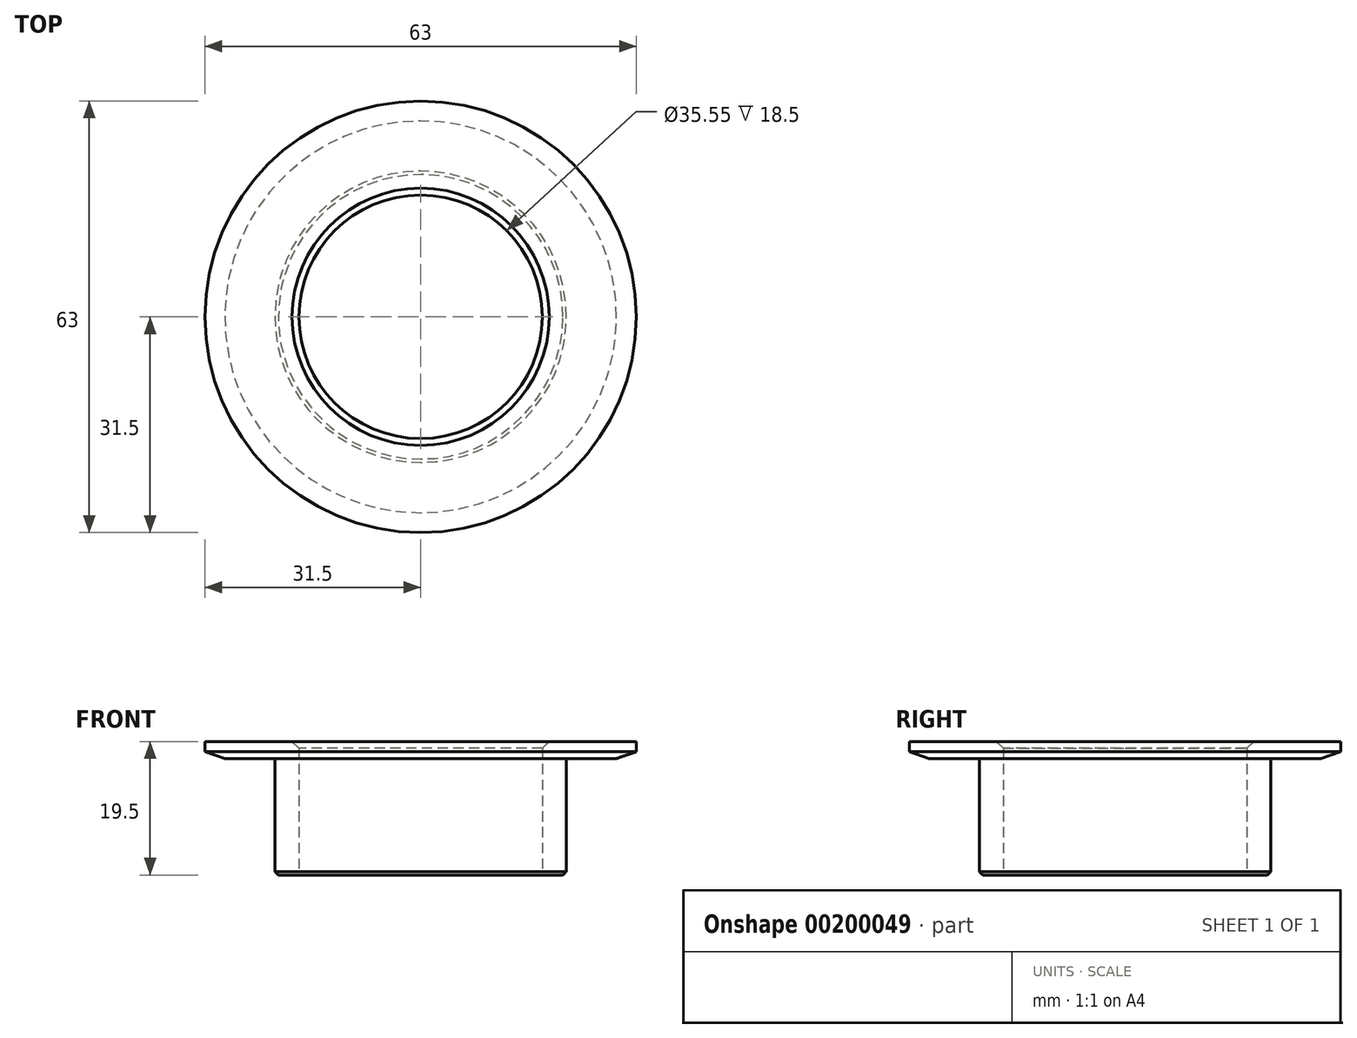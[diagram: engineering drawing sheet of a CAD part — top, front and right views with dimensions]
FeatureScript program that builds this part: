
annotation { "Feature Type Name" : "Feature", "Feature Type Description" : "" }
export const myFeature = defineFeature(function(context is Context, id is Id, definition is map)
    precondition{}
    {
        {
            var Q0;
            Q0=qCreatedBy(makeId("Top.planeOp"),FACE);
            var sketch = newSketch(context, id + "F0", { "sketchPlane" : qUnion([Q0])});
            skCircle(sketch, "E0", {"center": v(0, 0) * mm, "radius": 21.27 * mm});
            skCircle(sketch, "E1", {"center": v(0, 0) * mm, "radius": 17.77 * mm});
            skSolve(sketch);
        }
        {
            var Q0;
            Q0 = qSketchRegion(id + "F0", true);
            extrude(context, id + "F1", {"entities" : qUnion([Q0]), "depth" : 17 * mm});
        }
        {
            var Q0;
            Q0=makeQuery(id+"F1.opExtrude","CAP_FACE",FACE,{"disambiguationData":[OSD([sQuery(id+"F0.wireOp",EDGE,"E0"),sQuery(id+"F0.wireOp",EDGE,"E1")])],"isStart":false});
            var sketch = newSketch(context, id + "F2", { "sketchPlane" : qUnion([Q0])});
            skCircle(sketch, "E2", {"center": v(0, 0) * mm, "radius": 31.5 * mm});
            skCircle(sketch, "E3", {"center": v(0, 0) * mm, "radius": 17.77 * mm});
            skSolve(sketch);
        }
        {
            var Q0;
            Q0 = qSketchRegion(id + "F2", true);
            extrude(context, id + "F3", {"entities" : qUnion([Q0]), "operationType" : NewBodyOperationType.ADD, "depth" : 2.5 * mm});
        }
        {
            var Q0;
            Q0=makeQuery(id+"F3.opExtrude","CAP_EDGE",EDGE,{"disambiguationData":[OSD([sQuery(id+"F2.wireOp",EDGE,"E2")])],"isStart":true});
            chamfer(context, id + "F4", {"entities" : qUnion([Q0]), "chamferType" : ChamferType.TWO_OFFSETS, "width1" : 1 * mm, "oppositeDirection" : false, "width2" : 2.9 * mm, "tangentPropagation" : true});
        }
        {
            var Q0;
            Q0=makeQuery(id+"F1.opExtrude","CAP_EDGE",EDGE,{"disambiguationData":[OSD([sQuery(id+"F0.wireOp",EDGE,"E0")])],"isStart":true});
            chamfer(context, id + "F5", {"entities" : qUnion([Q0]), "width" : 0.5 * mm, "tangentPropagation" : true});
        }
        {
            var Q0;
            Q0=makeQuery(id+"F3.opExtrude","CAP_EDGE",EDGE,{"disambiguationData":[OSD([sQuery(id+"F2.wireOp",EDGE,"E3")])],"isStart":false});
            chamfer(context, id + "F6", {"entities" : qUnion([Q0]), "width" : 1 * mm, "tangentPropagation" : true});
        }
    });
